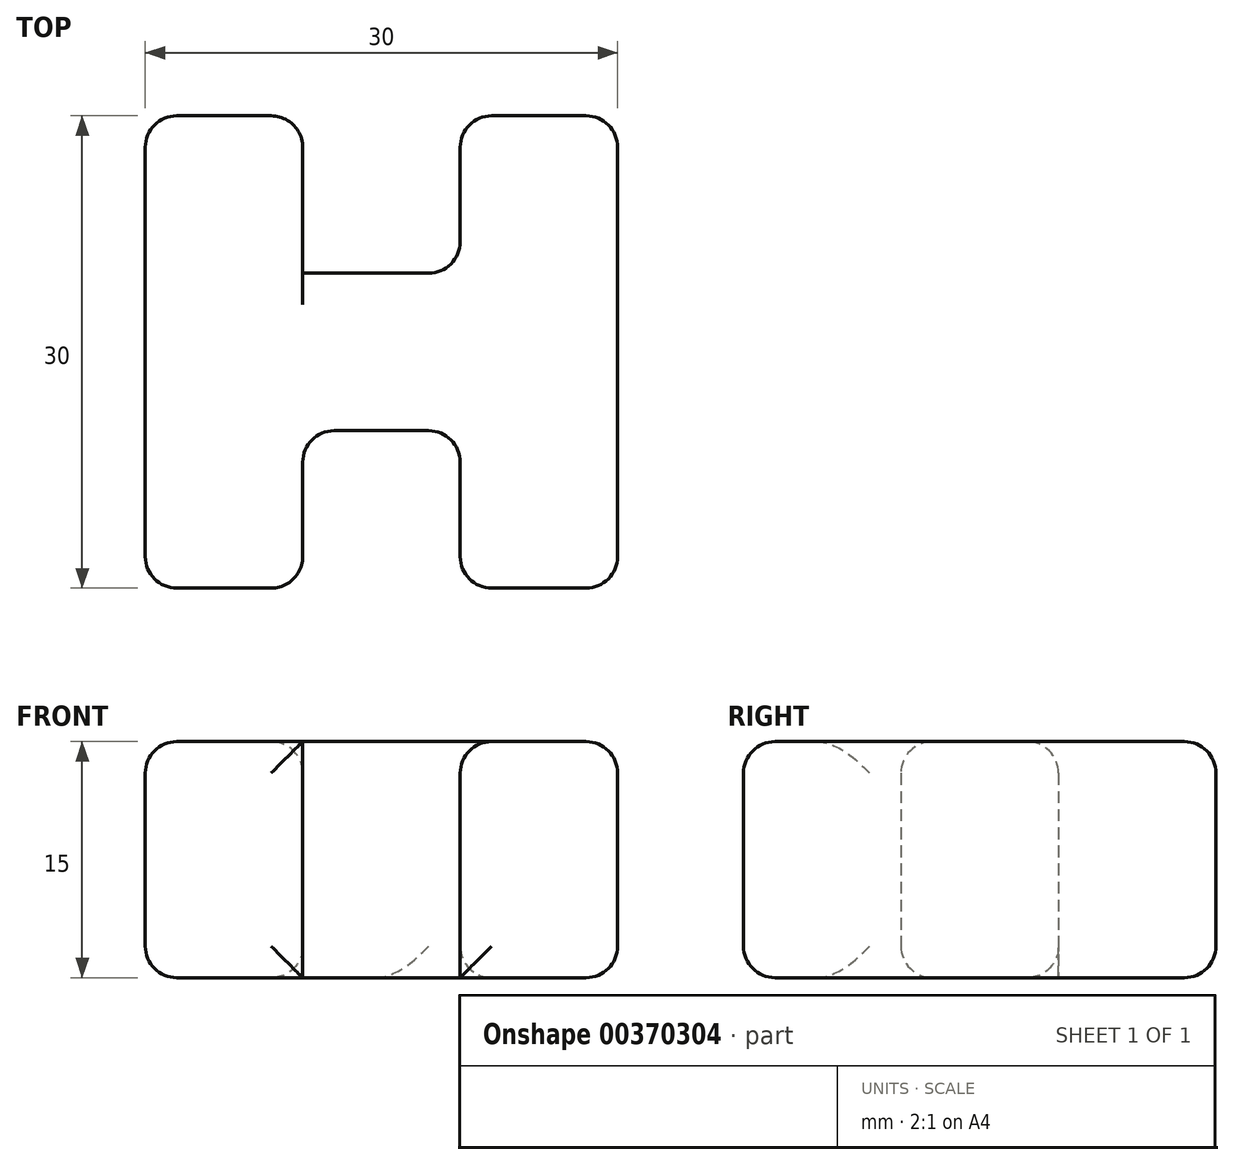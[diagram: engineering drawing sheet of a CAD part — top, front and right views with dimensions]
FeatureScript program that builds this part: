
annotation { "Feature Type Name" : "Feature", "Feature Type Description" : "" }
export const myFeature = defineFeature(function(context is Context, id is Id, definition is map)
    precondition{}
    {
        {
            var Q0;
            Q0=qCreatedBy(makeId("Top.planeOp"),FACE);
            var sketch = newSketch(context, id + "F0", { "sketchPlane" : qUnion([Q0])});
            skLineSegment(sketch, "E0", {"start": v(0, 0) * mm, "end": v(0, 30) * mm});
            skLineSegment(sketch, "E1", {"start": v(0, 30) * mm, "end": v(10, 30) * mm});
            skLineSegment(sketch, "E2", {"start": v(0, 0) * mm, "end": v(10, 0) * mm});
            skLineSegment(sketch, "E3", {"start": v(10, 0) * mm, "end": v(10, 30) * mm});
            skLineSegment(sketch, "E4", {"start": v(10, 0) * mm, "end": v(10, 10) * mm});
            skLineSegment(sketch, "E5", {"start": v(10, 10) * mm, "end": v(20, 10) * mm});
            skLineSegment(sketch, "E6", {"start": v(20, 10) * mm, "end": v(20, 20) * mm});
            skLineSegment(sketch, "E7", {"start": v(20, 20) * mm, "end": v(10, 20) * mm});
            skLineSegment(sketch, "E8", {"start": v(10, 20) * mm, "end": v(10, 30) * mm});
            skLineSegment(sketch, "E9", {"start": v(20, 30) * mm, "end": v(20, 20) * mm});
            skLineSegment(sketch, "E10", {"start": v(20, 0) * mm, "end": v(20, 10) * mm});
            skLineSegment(sketch, "E11", {"start": v(30, 0) * mm, "end": v(20, 0) * mm});
            skLineSegment(sketch, "E12", {"start": v(30, 0) * mm, "end": v(30, 30) * mm});
            skLineSegment(sketch, "E13", {"start": v(30, 30) * mm, "end": v(20, 30) * mm});
            skSolve(sketch);
        }
        {
            var Q0;
            Q0 = qSketchRegion(id + "F0", true);
            extrude(context, id + "F1", {"entities" : qUnion([Q0]), "depth" : 15 * mm});
        }
        {
            var Q0;
            Q0=makeQuery(id+"F1.opExtrude","SWEPT_EDGE",EDGE,{"disambiguationData":[OSD([sQuery(id+"F0.wireOp",EDGE,"E0"),sQuery(id+"F0.wireOp",EDGE,"E1")])]});
            var Q1;
            Q1=makeQuery(id+"F1.opExtrude","SWEPT_EDGE",EDGE,{"disambiguationData":[OSD([sQuery(id+"F0.wireOp",EDGE,"E9"),sQuery(id+"F0.wireOp",EDGE,"E13")])]});
            var Q2;
            Q2=makeQuery(id+"F1.opExtrude","SWEPT_FACE",FACE,{"disambiguationData":[OSD([sQuery(id+"F0.wireOp",EDGE,"E2")])]});
            var Q3;
            Q3=makeQuery(id+"F1.opExtrude","SWEPT_FACE",FACE,{"disambiguationData":[OSD([sQuery(id+"F0.wireOp",EDGE,"E11")])]});
            var Q4;
            Q4=makeQuery(id+"F1.opExtrude","SWEPT_EDGE",EDGE,{"disambiguationData":[OSD([sQuery(id+"F0.wireOp",EDGE,"E2"),sQuery(id+"F0.wireOp",EDGE,"E4")])]});
            var Q5;
            Q5=makeQuery(id+"F1.opExtrude","SWEPT_FACE",FACE,{"disambiguationData":[OSD([sQuery(id+"F0.wireOp",EDGE,"E8")])]});
            var Q6;
            Q6=makeQuery(id+"F1.opExtrude","SWEPT_FACE",FACE,{"disambiguationData":[OSD([sQuery(id+"F0.wireOp",EDGE,"E9")])]});
            var Q7;
            Q7=makeQuery(id+"F1.opExtrude","SWEPT_FACE",FACE,{"disambiguationData":[OSD([sQuery(id+"F0.wireOp",EDGE,"E13")])]});
            var Q8;
            Q8=makeQuery(id+"F1.opExtrude","CAP_EDGE",EDGE,{"disambiguationData":[OSD([sQuery(id+"F0.wireOp",EDGE,"E12")])],"isStart":false});
            var Q9;
            Q9=makeQuery(id+"F1.opExtrude","SWEPT_FACE",FACE,{"disambiguationData":[OSD([sQuery(id+"F0.wireOp",EDGE,"E4")])]});
            var Q10;
            Q10=makeQuery(id+"F1.opExtrude","CAP_EDGE",EDGE,{"disambiguationData":[OSD([sQuery(id+"F0.wireOp",EDGE,"E13")])],"isStart":false});
            var Q11;
            Q11=makeQuery(id+"F1.opExtrude","SWEPT_FACE",FACE,{"disambiguationData":[OSD([sQuery(id+"F0.wireOp",EDGE,"E1")])]});
            var Q12;
            Q12=makeQuery(id+"F1.opExtrude","CAP_EDGE",EDGE,{"disambiguationData":[OSD([sQuery(id+"F0.wireOp",EDGE,"E7")])],"isStart":false});
            var Q13;
            Q13=makeQuery(id+"F1.opExtrude","SWEPT_FACE",FACE,{"disambiguationData":[OSD([sQuery(id+"F0.wireOp",EDGE,"E5")])]});
            var Q14;
            Q14=makeQuery(id+"F1.opExtrude","CAP_EDGE",EDGE,{"disambiguationData":[OSD([sQuery(id+"F0.wireOp",EDGE,"E10")])],"isStart":false});
            var Q15;
            Q15=makeQuery(id+"F1.opExtrude","CAP_EDGE",EDGE,{"disambiguationData":[OSD([sQuery(id+"F0.wireOp",EDGE,"E4")])],"isStart":false});
            var Q16;
            Q16=makeQuery(id+"F1.opExtrude","SWEPT_FACE",FACE,{"disambiguationData":[OSD([sQuery(id+"F0.wireOp",EDGE,"E0")])]});
            var Q17;
            Q17=makeQuery(id+"F1.opExtrude","SWEPT_FACE",FACE,{"disambiguationData":[OSD([sQuery(id+"F0.wireOp",EDGE,"E12")])]});
            fillet(context, id + "F2", {"entities" : qUnion([Q0, Q1, Q2, Q3, Q4, Q5, Q6, Q7, Q8, Q9, Q10, Q11, Q12, Q13, Q14, Q15, Q16, Q17]), "radius" : 2 * mm, "tangentPropagation" : true, "allowEdgeOverflow" : false});
        }
    });
